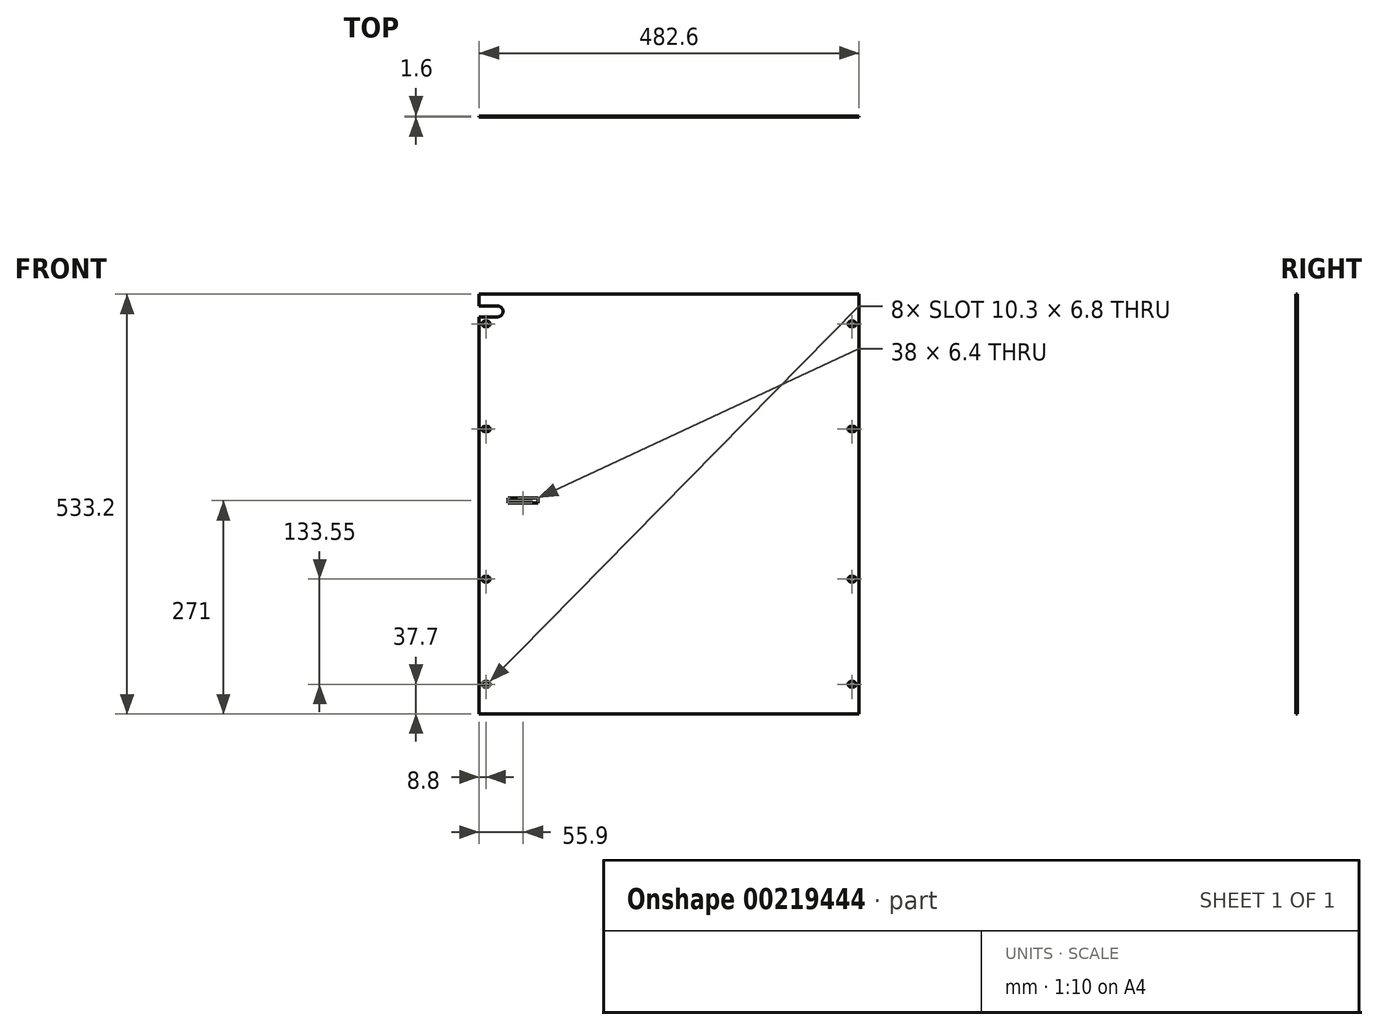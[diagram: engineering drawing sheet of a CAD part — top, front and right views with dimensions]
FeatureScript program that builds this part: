
annotation { "Feature Type Name" : "Feature", "Feature Type Description" : "" }
export const myFeature = defineFeature(function(context is Context, id is Id, definition is map)
    precondition{}
    {
        {
            var Q0;
            Q0=qCreatedBy(makeId("Front.planeOp"),FACE);
            var sketch = newSketch(context, id + "F0", { "sketchPlane" : qUnion([Q0])});
            skLineSegment(sketch, "E0.bottom", {"start": v(-241.3, 266.6) * mm, "end": v(241.3, 266.6) * mm});
            skLineSegment(sketch, "E0.top", {"start": v(-241.3, -266.6) * mm, "end": v(241.3, -266.6) * mm});
            skLineSegment(sketch, "E0.left", {"start": v(-241.3, 266.6) * mm, "end": v(-241.3, -266.6) * mm});
            skLineSegment(sketch, "E0.right", {"start": v(241.3, 266.6) * mm, "end": v(241.3, -266.6) * mm});
            skPoint(sketch, "E0.middle", {"position": v(0, 0) * mm});
            skSolve(sketch);
        }
        {
            var Q0;
            Q0=qSketchRegion(id+"F0",true);
            extrude(context, id + "F1", {"entities" : qUnion([Q0]), "oppositeDirection" : true, "depth" : 1.6 * mm});
        }
        {
            var Q0;
            Q0=makeQuery(id+"F1.opExtrude","CAP_FACE",FACE,{"disambiguationData":[OSD([sQuery(id+"F0.wireOp",EDGE,"E0.bottom"),sQuery(id+"F0.wireOp",EDGE,"E0.top"),sQuery(id+"F0.wireOp",EDGE,"E0.left"),sQuery(id+"F0.wireOp",EDGE,"E0.right")])],"isStart":true});
            var sketch = newSketch(context, id + "F2", { "sketchPlane" : qUnion([Q0])});
            skLineSegment(sketch, "E1.bottom", {"start": v(-230.75, 225.5) * mm, "end": v(-234.25, 225.5) * mm});
            skLineSegment(sketch, "E1.top", {"start": v(-230.75, 232.3) * mm, "end": v(-234.25, 232.3) * mm});
            skLineSegment(sketch, "E1.left", {"start": v(-230.75, 225.5) * mm, "end": v(-230.75, 232.3) * mm});
            skLineSegment(sketch, "E1.right", {"start": v(-234.25, 225.5) * mm, "end": v(-234.25, 232.3) * mm});
            skPoint(sketch, "E1.middle", {"position": v(-232.5, 228.9) * mm});
            skArc(sketch, "E2", {"start": v(-230.75, 225.5) * mm, "mid": v(-227.35, 228.9) * mm, "end": v(-230.75, 232.3) * mm});
            skArc(sketch, "E3", {"start": v(-234.25, 232.3) * mm, "mid": v(-237.65, 228.9) * mm, "end": v(-234.25, 225.5) * mm});
            skSolve(sketch);
        }
        {
            var Q0;
            Q0=makeQuery(id+"F2.imprint","IMPRINT",FACE,{"disambiguationData":[TD([[makeQuery(id+"F2.imprint","IMPRINT",EDGE,{"derivedFrom":sQuery(id+"F2.wireOp",EDGE,"E1.bottom")}),1.0]])]});
            var sketch = newSketch(context, id + "F3", { "sketchPlane" : qUnion([Q0])});
            skLineSegment(sketch, "E4.bottom", {"start": v(-230.75, 91.95) * mm, "end": v(-234.25, 91.95) * mm});
            skLineSegment(sketch, "E4.top", {"start": v(-230.75, 98.75) * mm, "end": v(-234.25, 98.75) * mm});
            skLineSegment(sketch, "E4.left", {"start": v(-230.75, 91.95) * mm, "end": v(-230.75, 98.75) * mm});
            skLineSegment(sketch, "E4.right", {"start": v(-234.25, 91.95) * mm, "end": v(-234.25, 98.75) * mm});
            skPoint(sketch, "E4.middle", {"position": v(-232.5, 95.35) * mm});
            skArc(sketch, "E5", {"start": v(-230.75, 91.95) * mm, "mid": v(-227.35, 95.35) * mm, "end": v(-230.75, 98.75) * mm});
            skArc(sketch, "E6", {"start": v(-234.25, 98.75) * mm, "mid": v(-237.65, 95.35) * mm, "end": v(-234.25, 91.95) * mm});
            skSolve(sketch);
        }
        {
            var Q0;
            Q0=makeQuery(id+"F2.imprint","IMPRINT",FACE,{"disambiguationData":[TD([[makeQuery(id+"F2.imprint","IMPRINT",EDGE,{"derivedFrom":sQuery(id+"F2.wireOp",EDGE,"E1.bottom")}),1.0]])]});
            var sketch = newSketch(context, id + "F4", { "sketchPlane" : qUnion([Q0])});
            skLineSegment(sketch, "E7.bottom", {"start": v(-230.75, -98.75) * mm, "end": v(-234.25, -98.75) * mm});
            skLineSegment(sketch, "E7.top", {"start": v(-230.75, -91.95) * mm, "end": v(-234.25, -91.95) * mm});
            skLineSegment(sketch, "E7.left", {"start": v(-230.75, -98.75) * mm, "end": v(-230.75, -91.95) * mm});
            skLineSegment(sketch, "E7.right", {"start": v(-234.25, -98.75) * mm, "end": v(-234.25, -91.95) * mm});
            skPoint(sketch, "E7.middle", {"position": v(-232.5, -95.35) * mm});
            skArc(sketch, "E8", {"start": v(-230.75, -98.75) * mm, "mid": v(-227.35, -95.35) * mm, "end": v(-230.75, -91.95) * mm});
            skArc(sketch, "E9", {"start": v(-234.25, -91.95) * mm, "mid": v(-237.65, -95.35) * mm, "end": v(-234.25, -98.75) * mm});
            skSolve(sketch);
        }
        {
            var Q0;
            Q0=makeQuery(id+"F2.imprint","IMPRINT",FACE,{"disambiguationData":[TD([[makeQuery(id+"F2.imprint","IMPRINT",EDGE,{"derivedFrom":sQuery(id+"F2.wireOp",EDGE,"E1.bottom")}),1.0]])]});
            var sketch = newSketch(context, id + "F5", { "sketchPlane" : qUnion([Q0])});
            skLineSegment(sketch, "E10.bottom", {"start": v(-230.75, -232.3) * mm, "end": v(-234.25, -232.3) * mm});
            skLineSegment(sketch, "E10.top", {"start": v(-230.75, -225.5) * mm, "end": v(-234.25, -225.5) * mm});
            skLineSegment(sketch, "E10.left", {"start": v(-230.75, -232.3) * mm, "end": v(-230.75, -225.5) * mm});
            skLineSegment(sketch, "E10.right", {"start": v(-234.25, -232.3) * mm, "end": v(-234.25, -225.5) * mm});
            skPoint(sketch, "E10.middle", {"position": v(-232.5, -228.9) * mm});
            skArc(sketch, "E11", {"start": v(-230.75, -232.3) * mm, "mid": v(-227.35, -228.9) * mm, "end": v(-230.75, -225.5) * mm});
            skArc(sketch, "E12", {"start": v(-234.25, -225.5) * mm, "mid": v(-237.65, -228.9) * mm, "end": v(-234.25, -232.3) * mm});
            skSolve(sketch);
        }
        {
            var Q0;
            Q0=makeQuery(id+"F1.opExtrude","CAP_FACE",FACE,{"disambiguationData":[OSD([sQuery(id+"F0.wireOp",EDGE,"E0.bottom"),sQuery(id+"F0.wireOp",EDGE,"E0.top"),sQuery(id+"F0.wireOp",EDGE,"E0.left"),sQuery(id+"F0.wireOp",EDGE,"E0.right")])],"isStart":true});
            var sketch = newSketch(context, id + "F6", { "sketchPlane" : qUnion([Q0])});
            skLineSegment(sketch, "E13.bottom", {"start": v(234.25, 225.5) * mm, "end": v(230.75, 225.5) * mm});
            skLineSegment(sketch, "E13.top", {"start": v(234.25, 232.3) * mm, "end": v(230.75, 232.3) * mm});
            skLineSegment(sketch, "E13.left", {"start": v(234.25, 225.5) * mm, "end": v(234.25, 232.3) * mm});
            skLineSegment(sketch, "E13.right", {"start": v(230.75, 225.5) * mm, "end": v(230.75, 232.3) * mm});
            skPoint(sketch, "E13.middle", {"position": v(232.5, 228.9) * mm});
            skArc(sketch, "E14", {"start": v(234.25, 225.5) * mm, "mid": v(237.65, 228.9) * mm, "end": v(234.25, 232.3) * mm});
            skArc(sketch, "E15", {"start": v(230.75, 232.3) * mm, "mid": v(227.35, 228.9) * mm, "end": v(230.75, 225.5) * mm});
            skSolve(sketch);
        }
        {
            var Q0;
            Q0=makeQuery(id+"F6.imprint","IMPRINT",FACE,{"disambiguationData":[TD([[makeQuery(id+"F6.imprint","IMPRINT",EDGE,{"derivedFrom":sQuery(id+"F6.wireOp",EDGE,"E13.bottom")}),1.0]])]});
            var sketch = newSketch(context, id + "F7", { "sketchPlane" : qUnion([Q0])});
            skLineSegment(sketch, "E16.bottom", {"start": v(234.25, 91.95) * mm, "end": v(230.75, 91.95) * mm});
            skLineSegment(sketch, "E16.top", {"start": v(234.25, 98.75) * mm, "end": v(230.75, 98.75) * mm});
            skLineSegment(sketch, "E16.left", {"start": v(234.25, 91.95) * mm, "end": v(234.25, 98.75) * mm});
            skLineSegment(sketch, "E16.right", {"start": v(230.75, 91.95) * mm, "end": v(230.75, 98.75) * mm});
            skPoint(sketch, "E16.middle", {"position": v(232.5, 95.35) * mm});
            skArc(sketch, "E17", {"start": v(234.25, 91.95) * mm, "mid": v(237.65, 95.35) * mm, "end": v(234.25, 98.75) * mm});
            skArc(sketch, "E18", {"start": v(230.75, 98.75) * mm, "mid": v(227.35, 95.35) * mm, "end": v(230.75, 91.95) * mm});
            skSolve(sketch);
        }
        {
            var Q0;
            Q0=makeQuery(id+"F6.imprint","IMPRINT",FACE,{"disambiguationData":[TD([[makeQuery(id+"F6.imprint","IMPRINT",EDGE,{"derivedFrom":sQuery(id+"F6.wireOp",EDGE,"E13.bottom")}),1.0]])]});
            var sketch = newSketch(context, id + "F8", { "sketchPlane" : qUnion([Q0])});
            skLineSegment(sketch, "E19.bottom", {"start": v(234.25, -98.75) * mm, "end": v(230.75, -98.75) * mm});
            skLineSegment(sketch, "E19.top", {"start": v(234.25, -91.95) * mm, "end": v(230.75, -91.95) * mm});
            skLineSegment(sketch, "E19.left", {"start": v(234.25, -98.75) * mm, "end": v(234.25, -91.95) * mm});
            skLineSegment(sketch, "E19.right", {"start": v(230.75, -98.75) * mm, "end": v(230.75, -91.95) * mm});
            skPoint(sketch, "E19.middle", {"position": v(232.5, -95.35) * mm});
            skArc(sketch, "E20", {"start": v(230.75, -91.95) * mm, "mid": v(227.35, -95.35) * mm, "end": v(230.75, -98.75) * mm});
            skArc(sketch, "E21", {"start": v(234.25, -98.75) * mm, "mid": v(237.65, -95.35) * mm, "end": v(234.25, -91.95) * mm});
            skSolve(sketch);
        }
        {
            var Q0;
            Q0=makeQuery(id+"F6.imprint","IMPRINT",FACE,{"disambiguationData":[TD([[makeQuery(id+"F6.imprint","IMPRINT",EDGE,{"derivedFrom":sQuery(id+"F6.wireOp",EDGE,"E13.bottom")}),1.0]])]});
            var sketch = newSketch(context, id + "F9", { "sketchPlane" : qUnion([Q0])});
            skLineSegment(sketch, "E22.bottom", {"start": v(234.25, -232.3) * mm, "end": v(230.75, -232.3) * mm});
            skLineSegment(sketch, "E22.top", {"start": v(234.25, -225.5) * mm, "end": v(230.75, -225.5) * mm});
            skLineSegment(sketch, "E22.left", {"start": v(234.25, -232.3) * mm, "end": v(234.25, -225.5) * mm});
            skLineSegment(sketch, "E22.right", {"start": v(230.75, -232.3) * mm, "end": v(230.75, -225.5) * mm});
            skPoint(sketch, "E22.middle", {"position": v(232.5, -228.9) * mm});
            skArc(sketch, "E23", {"start": v(234.25, -232.3) * mm, "mid": v(237.65, -228.9) * mm, "end": v(234.25, -225.5) * mm});
            skArc(sketch, "E24", {"start": v(230.75, -225.5) * mm, "mid": v(227.35, -228.9) * mm, "end": v(230.75, -232.3) * mm});
            skSolve(sketch);
        }
        {
            var Q0;
            Q0=makeQuery(id+"F1.opExtrude","CAP_FACE",FACE,{"disambiguationData":[OSD([sQuery(id+"F0.wireOp",EDGE,"E0.bottom"),sQuery(id+"F0.wireOp",EDGE,"E0.top"),sQuery(id+"F0.wireOp",EDGE,"E0.left"),sQuery(id+"F0.wireOp",EDGE,"E0.right")])],"isStart":true});
            var sketch = newSketch(context, id + "F10", { "sketchPlane" : qUnion([Q0])});
            skLineSegment(sketch, "E25.bottom", {"start": v(-166.4, 1.2) * mm, "end": v(-204.4, 1.2) * mm});
            skLineSegment(sketch, "E25.top", {"start": v(-166.4, 7.6) * mm, "end": v(-204.4, 7.6) * mm});
            skLineSegment(sketch, "E25.left", {"start": v(-166.4, 1.2) * mm, "end": v(-166.4, 7.6) * mm});
            skLineSegment(sketch, "E25.right", {"start": v(-204.4, 1.2) * mm, "end": v(-204.4, 7.6) * mm});
            skPoint(sketch, "E25.middle", {"position": v(-185.4, 4.4) * mm});
            skSolve(sketch);
        }
        {
            var Q0;
            Q0=qSketchRegion(id+"F10",true);
            extrude(context, id + "F11", {"entities" : qUnion([Q0]), "operationType" : NewBodyOperationType.REMOVE, "oppositeDirection" : true, "depth" : 1.6 * mm});
        }
        {
            var Q0;
            Q0=qSketchRegion(id+"F2",true);
            var Q1;
            Q1=qSketchRegion(id+"F3",true);
            var Q2;
            Q2=qSketchRegion(id+"F4",true);
            var Q3;
            Q3=qSketchRegion(id+"F5",true);
            var Q4;
            Q4=qSketchRegion(id+"F6",true);
            var Q5;
            Q5=qSketchRegion(id+"F7",true);
            var Q6;
            Q6=qSketchRegion(id+"F8",true);
            var Q7;
            Q7=qSketchRegion(id+"F9",true);
            extrude(context, id + "F12", {"entities" : qUnion([Q0, Q1, Q2, Q3, Q4, Q5, Q6, Q7]), "operationType" : NewBodyOperationType.REMOVE, "oppositeDirection" : true, "depth" : 1.6 * mm});
        }
        {
            var Q0;
            Q0=makeQuery(id+"F1.opExtrude","CAP_FACE",FACE,{"disambiguationData":[OSD([sQuery(id+"F0.wireOp",EDGE,"E0.bottom"),sQuery(id+"F0.wireOp",EDGE,"E0.top"),sQuery(id+"F0.wireOp",EDGE,"E0.left"),sQuery(id+"F0.wireOp",EDGE,"E0.right")])],"isStart":true});
            var sketch = newSketch(context, id + "F13", { "sketchPlane" : qUnion([Q0])});
            skCircle(sketch, "E26", {"center": v(-218, 244.8) * mm, "radius": 7 * mm});
            skLineSegment(sketch, "E27.bottom", {"start": v(-218, 251.8) * mm, "end": v(-241.3, 251.8) * mm});
            skLineSegment(sketch, "E27.top", {"start": v(-218, 237.8) * mm, "end": v(-241.3, 237.8) * mm});
            skLineSegment(sketch, "E27.left", {"start": v(-218, 251.8) * mm, "end": v(-218, 237.8) * mm});
            skLineSegment(sketch, "E27.right", {"start": v(-241.3, 251.8) * mm, "end": v(-241.3, 237.8) * mm});
            skPoint(sketch, "E27.middle", {"position": v(-229.65, 244.8) * mm});
            skSolve(sketch);
        }
        {
            var Q0;
            Q0=makeQuery(id+"F13.imprint","IMPRINT",FACE,{"disambiguationData":[TD([[makeQuery(id+"F13.imprint","IMPRINT",EDGE,{"derivedFrom":sQuery(id+"F13.wireOp",EDGE,"E26")}),1.0]])]});
            var Q1;
            {var subQ1=sQuery(id+"F13.wireOp",EDGE,"E27.bottom");Q1=makeQuery(id+"F13.imprint","IMPRINT",FACE,{"disambiguationData":[TD([[makeQuery(id+"F13.imprint","IMPRINT",EDGE,{"derivedFrom":subQ1}),1.0]])]});}
            extrude(context, id + "F14", {"entities" : qUnion([Q0, Q1]), "operationType" : NewBodyOperationType.REMOVE, "oppositeDirection" : true, "depth" : 1.6 * mm});
        }
    });
